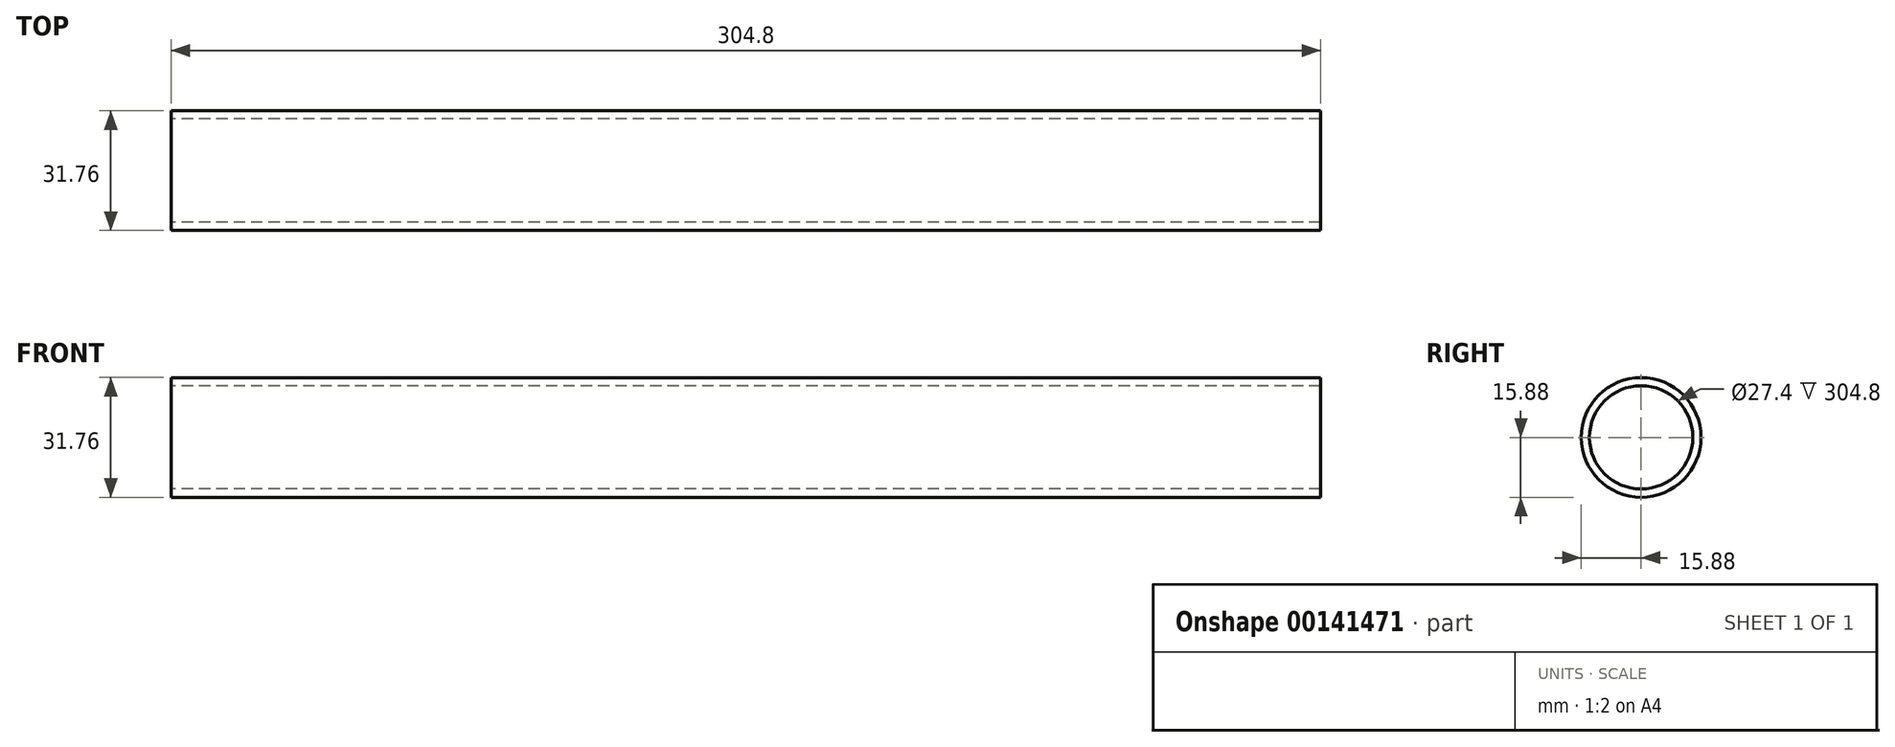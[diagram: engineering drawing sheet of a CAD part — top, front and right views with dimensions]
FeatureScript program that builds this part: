
annotation { "Feature Type Name" : "Feature", "Feature Type Description" : "" }
export const myFeature = defineFeature(function(context is Context, id is Id, definition is map)
    precondition{}
    {
        {
            var Q0;
            Q0=qCreatedBy(makeId("Right.planeOp"),FACE);
            var sketch = newSketch(context, id + "F0", { "sketchPlane" : qUnion([Q0])});
            skCircle(sketch, "E0", {"center": v(0, 0) * mm, "radius": 15.88 * mm});
            skCircle(sketch, "E1", {"center": v(0, 0) * mm, "radius": 13.7 * mm});
            skSolve(sketch);
        }
        {
            var Q0;
            Q0=makeQuery(id+"F0.imprint","IMPRINT",FACE,{"disambiguationData":[TD([[makeQuery(id+"F0.imprint","IMPRINT",EDGE,{"derivedFrom":sQuery(id+"F0.wireOp",EDGE,"E0")}),1.0]])]});
            extrude(context, id + "F1", {"entities" : qUnion([Q0]), "depth" : 304.8 * mm});
        }
    });
